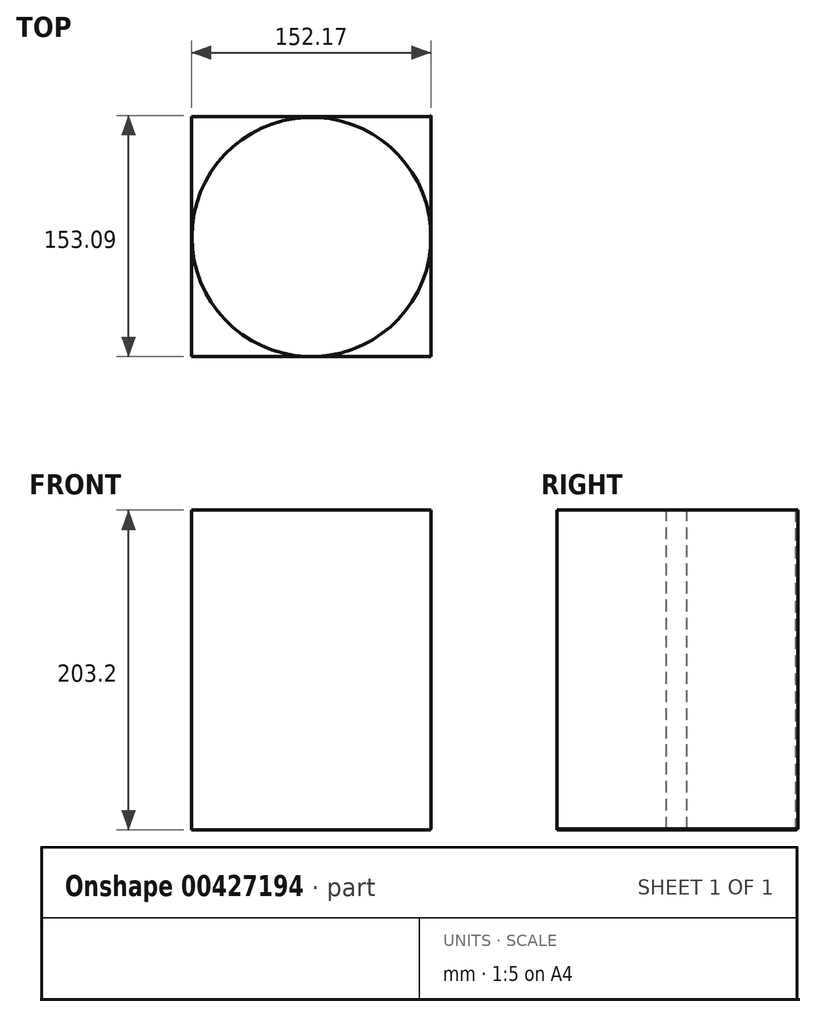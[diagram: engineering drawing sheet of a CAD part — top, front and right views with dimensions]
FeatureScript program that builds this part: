
annotation { "Feature Type Name" : "Feature", "Feature Type Description" : "" }
export const myFeature = defineFeature(function(context is Context, id is Id, definition is map)
    precondition{}
    {
        {
            var Q0;
            Q0=qCreatedBy(makeId("Top.planeOp"),FACE);
            var sketch = newSketch(context, id + "F0", { "sketchPlane" : qUnion([Q0])});
            skLineSegment(sketch, "E0.bottom", {"start": v(-76.25, 76.4) * mm, "end": v(75.66, 76.4) * mm});
            skLineSegment(sketch, "E0.top", {"start": v(-76.25, -75.96) * mm, "end": v(75.66, -75.96) * mm});
            skLineSegment(sketch, "E0.left", {"start": v(-76.25, 76.4) * mm, "end": v(-76.25, -75.96) * mm});
            skLineSegment(sketch, "E0.right", {"start": v(75.66, 76.4) * mm, "end": v(75.66, -75.96) * mm});
            skSolve(sketch);
        }
        {
            var Q0;
            Q0=makeQuery(id+"F0.imprint","IMPRINT",FACE,{"disambiguationData":[TD([[makeQuery(id+"F0.imprint","IMPRINT",EDGE,{"derivedFrom":sQuery(id+"F0.wireOp",EDGE,"E0.bottom")}),-1.0]])]});
            extrude(context, id + "F1", {"entities" : qUnion([Q0]), "depth" : 101.6 * mm, "hasSecondDirection" : true, "secondDirectionOppositeDirection" : true, "secondDirectionDepth" : 101.6 * mm});
        }
        {
            var Q0;
            Q0=makeQuery(id+"F1.opExtrude","CAP_FACE",FACE,{"disambiguationData":[OSD([sQuery(id+"F0.wireOp",EDGE,"E0.bottom"),sQuery(id+"F0.wireOp",EDGE,"E0.top"),sQuery(id+"F0.wireOp",EDGE,"E0.left"),sQuery(id+"F0.wireOp",EDGE,"E0.right")])],"isStart":false});
            var sketch = newSketch(context, id + "F2", { "sketchPlane" : qUnion([Q0])});
            skPoint(sketch, "E1", {"position": v(0, 0) * mm});
            skSolve(sketch);
        }
        {
            var Q0;
            Q0=sQuery(id+"F2.wireOp",VERTEX,"E1");
            var Q1;
            Q1=makeQuery(id+"F1.opExtrude","SWEPT_BODY",BODY,{"disambiguationData":[OSD([sQuery(id+"F0.wireOp",EDGE,"E0.bottom"),sQuery(id+"F0.wireOp",EDGE,"E0.top"),sQuery(id+"F0.wireOp",EDGE,"E0.left"),sQuery(id+"F0.wireOp",EDGE,"E0.right")])]});
            hole(context, id + "F3", {"style" : HoleStyle.SIMPLE, "endStyle" : HoleEndStyle.BLIND, "holeDiameter" : 151.9 * mm, "holeDepth" : 203.2 * mm, "isTappedThrough" : true, "tappedDepth" : 12.7 * mm, "tapClearance" : 3, "startFromSketch" : true, "locations" : qUnion([Q0]), "scope" : qUnion([Q1])});
        }
        {
            var Q0;
            {var subQ0=sQuery(id+"F0.wireOp",EDGE,"E0.right");var subQ2=sQuery(id+"F0.wireOp",EDGE,"E0.top");Q0=makeQuery(id+"F3.hole-0.boolean.opBoolean","SPLIT",FACE,{"disambiguationData":[TD([makeQuery(id+"F1.opExtrude","SWEPT_FACE",FACE,{"disambiguationData":[OSD([subQ2])]})])],"derivedFrom":makeQuery(id+"F1.opExtrude","SWEPT_FACE",FACE,{"disambiguationData":[OSD([subQ0])]})});}
            var sketch = newSketch(context, id + "F4", { "sketchPlane" : qUnion([Q0])});
            skLineSegment(sketch, "E2.bottom", {"start": v(-75.96, 101.6) * mm, "end": v(77.13, 101.6) * mm});
            skLineSegment(sketch, "E2.top", {"start": v(-75.96, -100.82) * mm, "end": v(77.13, -100.82) * mm});
            skLineSegment(sketch, "E2.left", {"start": v(-75.96, 101.6) * mm, "end": v(-75.96, -100.82) * mm});
            skLineSegment(sketch, "E2.right", {"start": v(77.13, 101.6) * mm, "end": v(77.13, -100.82) * mm});
            skSolve(sketch);
        }
        {
            var Q0;
            Q0 = qSketchRegion(id + "F4", true);
            extrude(context, id + "F5", {"entities" : qUnion([Q0]), "operationType" : NewBodyOperationType.ADD, "depth" : 0.25 * mm});
        }
    });
